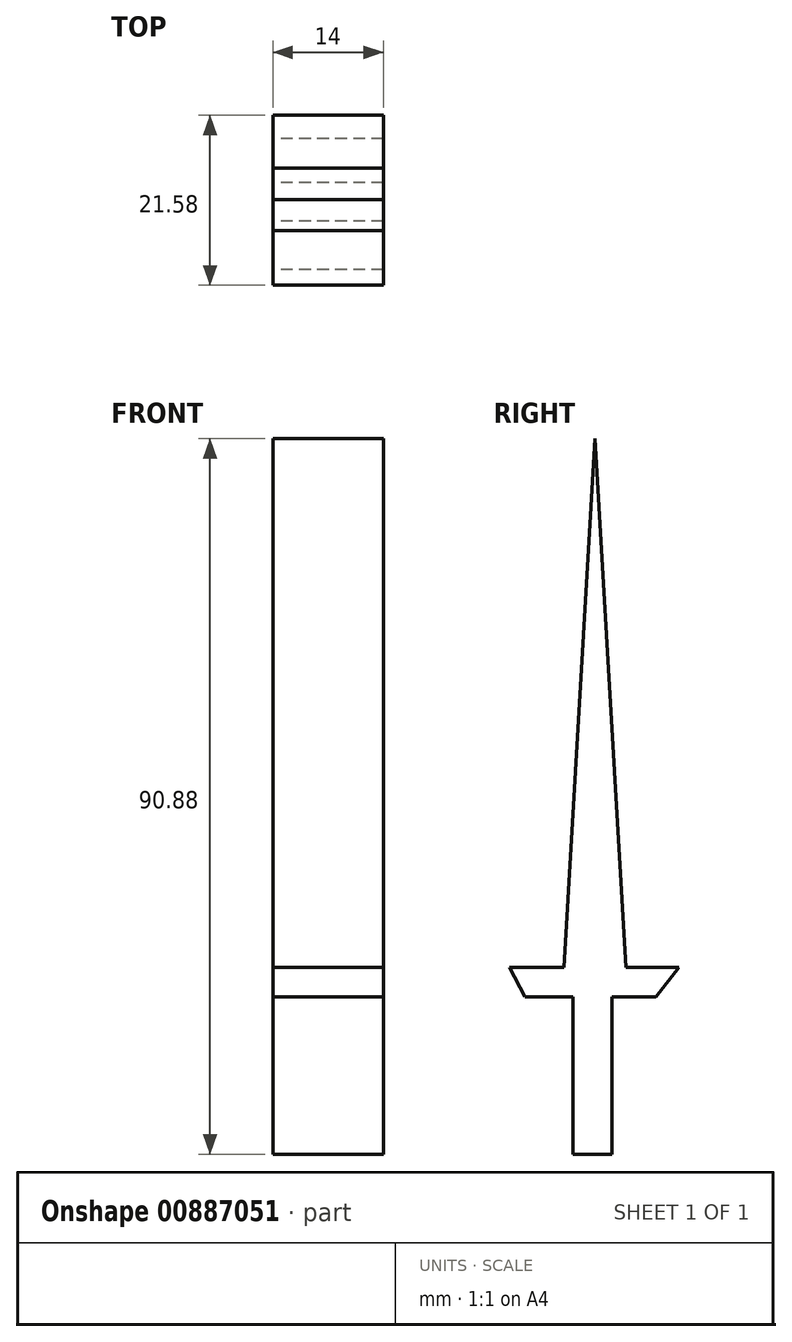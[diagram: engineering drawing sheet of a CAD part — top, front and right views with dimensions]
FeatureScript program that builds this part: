
annotation { "Feature Type Name" : "Feature", "Feature Type Description" : "" }
export const myFeature = defineFeature(function(context is Context, id is Id, definition is map)
    precondition{}
    {
        {
            var Q0;
            Q0=qCreatedBy(makeId("Right.planeOp"),FACE);
            var sketch = newSketch(context, id + "F0", { "sketchPlane" : qUnion([Q0])});
            skLineSegment(sketch, "E0", {"start": v(-10.9, 0) * mm, "end": v(10.7, 0) * mm});
            skLineSegment(sketch, "E1", {"start": v(-10.9, 0) * mm, "end": v(-8.91, -3.71) * mm});
            skLineSegment(sketch, "E2", {"start": v(-8.91, -3.71) * mm, "end": v(7.72, -3.71) * mm});
            skLineSegment(sketch, "E3", {"start": v(7.72, -3.71) * mm, "end": v(10.7, 0) * mm});
            skLineSegment(sketch, "E4", {"start": v(-2.77, -3.71) * mm, "end": v(-2.77, -23.71) * mm});
            skLineSegment(sketch, "E5", {"start": v(2.18, -3.71) * mm, "end": v(2.18, -23.71) * mm});
            skLineSegment(sketch, "E6", {"start": v(-2.77, -23.71) * mm, "end": v(2.18, -23.71) * mm});
            skLineSegment(sketch, "E7", {"start": v(-2.77, -3.71) * mm, "end": v(2.18, -6.49) * mm});
            skLineSegment(sketch, "E8", {"start": v(2.18, -6.49) * mm, "end": v(-2.77, -9.36) * mm});
            skLineSegment(sketch, "E9", {"start": v(-2.77, -9.36) * mm, "end": v(2.18, -11.83) * mm});
            skLineSegment(sketch, "E10", {"start": v(2.18, -11.83) * mm, "end": v(-2.77, -13.71) * mm});
            skLineSegment(sketch, "E11", {"start": v(-2.77, -13.71) * mm, "end": v(2.18, -16.98) * mm});
            skLineSegment(sketch, "E12", {"start": v(2.18, -16.98) * mm, "end": v(-2.77, -19.75) * mm});
            skLineSegment(sketch, "E13", {"start": v(-2.77, -19.75) * mm, "end": v(2.18, -21.34) * mm});
            skLineSegment(sketch, "E14", {"start": v(2.18, -21.34) * mm, "end": v(-2.77, -23.71) * mm});
            skLineSegment(sketch, "E15", {"start": v(2.18, -23.71) * mm, "end": v(-2.77, -21.34) * mm});
            skLineSegment(sketch, "E16", {"start": v(-2.77, -21.34) * mm, "end": v(2.18, -19.75) * mm});
            skLineSegment(sketch, "E17", {"start": v(2.18, -19.75) * mm, "end": v(-2.77, -16.98) * mm});
            skLineSegment(sketch, "E18", {"start": v(-2.77, -16.98) * mm, "end": v(2.18, -13.71) * mm});
            skLineSegment(sketch, "E19", {"start": v(2.18, -13.71) * mm, "end": v(-2.77, -12.03) * mm});
            skLineSegment(sketch, "E20", {"start": v(-2.77, -12.03) * mm, "end": v(2.18, -8.86) * mm});
            skLineSegment(sketch, "E21", {"start": v(2.18, -8.86) * mm, "end": v(-2.77, -6.39) * mm});
            skLineSegment(sketch, "E22", {"start": v(-2.77, -6.39) * mm, "end": v(2.18, -3.71) * mm});
            skLineSegment(sketch, "E23", {"start": v(-3.96, 0) * mm, "end": v(0, 67.17) * mm});
            skLineSegment(sketch, "E24.MirrorCS", {"start": v(3.96, 0) * mm, "end": v(0, 67.17) * mm});
            skSolve(sketch);
        }
        {
            var Q0;
            {var subQ0=sQuery(id+"F0.wireOp",EDGE,"E23");Q0=makeQuery(id+"F0.imprint","IMPRINT",FACE,{"disambiguationData":[TD([[makeQuery(id+"F0.imprint","IMPRINT",EDGE,{"derivedFrom":subQ0}),-1.0]])]});}
            var Q1;
            {var subQ0=sQuery(id+"F0.wireOp",EDGE,"E1");Q1=makeQuery(id+"F0.imprint","IMPRINT",FACE,{"disambiguationData":[TD([[makeQuery(id+"F0.imprint","IMPRINT",EDGE,{"derivedFrom":subQ0}),1.0]])]});}
            var Q2;
            {var subQ0=sQuery(id+"F0.wireOp",EDGE,"E7");var subQ3=sQuery(id+"F0.wireOp",EDGE,"E22");var subQ5=makeQuery(id+"F0.imprint","INTERSECT",VERTEX,{"derivedFrom":[subQ0,subQ3]});Q2=makeQuery(id+"F0.imprint","IMPRINT",FACE,{"disambiguationData":[TD([[makeQuery(id+"F0.imprint","IMPRINT",EDGE,{"disambiguationData":[TD([[subQ5,1.0]])],"derivedFrom":subQ0}),1.0]])]});}
            var Q3;
            {var subQ1=sQuery(id+"F0.wireOp",EDGE,"E7");var subQ3=sQuery(id+"F0.wireOp",EDGE,"E22");var subQ4=makeQuery(id+"F0.imprint","INTERSECT",VERTEX,{"derivedFrom":[subQ1,subQ3]});Q3=makeQuery(id+"F0.imprint","IMPRINT",FACE,{"disambiguationData":[TD([[makeQuery(id+"F0.imprint","IMPRINT",EDGE,{"disambiguationData":[TD([[subQ4,-1.0]])],"derivedFrom":subQ1}),-1.0]])]});}
            var Q4;
            {var subQ0=sQuery(id+"F0.wireOp",EDGE,"E7");var subQ3=sQuery(id+"F0.wireOp",EDGE,"E22");var subQ5=makeQuery(id+"F0.imprint","INTERSECT",VERTEX,{"derivedFrom":[subQ0,subQ3]});Q4=makeQuery(id+"F0.imprint","IMPRINT",FACE,{"disambiguationData":[TD([[makeQuery(id+"F0.imprint","IMPRINT",EDGE,{"disambiguationData":[TD([[subQ5,1.0]])],"derivedFrom":subQ0}),-1.0]])]});}
            var Q5;
            {var subQ0=sQuery(id+"F0.wireOp",EDGE,"E22");var subQ3=sQuery(id+"F0.wireOp",EDGE,"E7");var subQ5=makeQuery(id+"F0.imprint","INTERSECT",VERTEX,{"derivedFrom":[subQ3,subQ0]});Q5=makeQuery(id+"F0.imprint","IMPRINT",FACE,{"disambiguationData":[TD([[makeQuery(id+"F0.imprint","IMPRINT",EDGE,{"disambiguationData":[TD([[subQ5,-1.0]])],"derivedFrom":subQ3}),1.0]])]});}
            var Q6;
            {var subQ0=sQuery(id+"F0.wireOp",EDGE,"E8");var subQ3=sQuery(id+"F0.wireOp",EDGE,"E21");var subQ5=makeQuery(id+"F0.imprint","INTERSECT",VERTEX,{"derivedFrom":[subQ0,subQ3]});Q6=makeQuery(id+"F0.imprint","IMPRINT",FACE,{"disambiguationData":[TD([[makeQuery(id+"F0.imprint","IMPRINT",EDGE,{"disambiguationData":[TD([[subQ5,-1.0]])],"derivedFrom":subQ0}),-1.0]])]});}
            var Q7;
            {var subQ0=sQuery(id+"F0.wireOp",EDGE,"E8");var subQ3=sQuery(id+"F0.wireOp",EDGE,"E21");var subQ5=makeQuery(id+"F0.imprint","INTERSECT",VERTEX,{"derivedFrom":[subQ0,subQ3]});Q7=makeQuery(id+"F0.imprint","IMPRINT",FACE,{"disambiguationData":[TD([[makeQuery(id+"F0.imprint","IMPRINT",EDGE,{"disambiguationData":[TD([[subQ5,1.0]])],"derivedFrom":subQ0}),1.0]])]});}
            var Q8;
            {var subQ1=sQuery(id+"F0.wireOp",EDGE,"E8");var subQ3=sQuery(id+"F0.wireOp",EDGE,"E21");var subQ4=makeQuery(id+"F0.imprint","INTERSECT",VERTEX,{"derivedFrom":[subQ1,subQ3]});Q8=makeQuery(id+"F0.imprint","IMPRINT",FACE,{"disambiguationData":[TD([[makeQuery(id+"F0.imprint","IMPRINT",EDGE,{"disambiguationData":[TD([[subQ4,-1.0]])],"derivedFrom":subQ1}),1.0]])]});}
            var Q9;
            {var subQ0=sQuery(id+"F0.wireOp",EDGE,"E9");var subQ3=sQuery(id+"F0.wireOp",EDGE,"E20");var subQ5=makeQuery(id+"F0.imprint","INTERSECT",VERTEX,{"derivedFrom":[subQ0,subQ3]});Q9=makeQuery(id+"F0.imprint","IMPRINT",FACE,{"disambiguationData":[TD([[makeQuery(id+"F0.imprint","IMPRINT",EDGE,{"disambiguationData":[TD([[subQ5,1.0]])],"derivedFrom":subQ0}),-1.0]])]});}
            var Q10;
            {var subQ0=sQuery(id+"F0.wireOp",EDGE,"E9");var subQ3=sQuery(id+"F0.wireOp",EDGE,"E20");var subQ5=makeQuery(id+"F0.imprint","INTERSECT",VERTEX,{"derivedFrom":[subQ0,subQ3]});Q10=makeQuery(id+"F0.imprint","IMPRINT",FACE,{"disambiguationData":[TD([[makeQuery(id+"F0.imprint","IMPRINT",EDGE,{"disambiguationData":[TD([[subQ5,-1.0]])],"derivedFrom":subQ0}),1.0]])]});}
            var Q11;
            {var subQ1=sQuery(id+"F0.wireOp",EDGE,"E9");var subQ3=sQuery(id+"F0.wireOp",EDGE,"E20");var subQ4=makeQuery(id+"F0.imprint","INTERSECT",VERTEX,{"derivedFrom":[subQ1,subQ3]});Q11=makeQuery(id+"F0.imprint","IMPRINT",FACE,{"disambiguationData":[TD([[makeQuery(id+"F0.imprint","IMPRINT",EDGE,{"disambiguationData":[TD([[subQ4,-1.0]])],"derivedFrom":subQ1}),-1.0]])]});}
            var Q12;
            {var subQ0=sQuery(id+"F0.wireOp",EDGE,"E10");var subQ3=sQuery(id+"F0.wireOp",EDGE,"E19");var subQ5=makeQuery(id+"F0.imprint","INTERSECT",VERTEX,{"derivedFrom":[subQ0,subQ3]});Q12=makeQuery(id+"F0.imprint","IMPRINT",FACE,{"disambiguationData":[TD([[makeQuery(id+"F0.imprint","IMPRINT",EDGE,{"disambiguationData":[TD([[subQ5,1.0]])],"derivedFrom":subQ0}),1.0]])]});}
            var Q13;
            {var subQ0=sQuery(id+"F0.wireOp",EDGE,"E10");var subQ3=sQuery(id+"F0.wireOp",EDGE,"E19");var subQ5=makeQuery(id+"F0.imprint","INTERSECT",VERTEX,{"derivedFrom":[subQ0,subQ3]});Q13=makeQuery(id+"F0.imprint","IMPRINT",FACE,{"disambiguationData":[TD([[makeQuery(id+"F0.imprint","IMPRINT",EDGE,{"disambiguationData":[TD([[subQ5,-1.0]])],"derivedFrom":subQ0}),-1.0]])]});}
            var Q14;
            {var subQ0=sQuery(id+"F0.wireOp",EDGE,"E11");var subQ3=sQuery(id+"F0.wireOp",EDGE,"E18");var subQ5=makeQuery(id+"F0.imprint","INTERSECT",VERTEX,{"derivedFrom":[subQ0,subQ3]});Q14=makeQuery(id+"F0.imprint","IMPRINT",FACE,{"disambiguationData":[TD([[makeQuery(id+"F0.imprint","IMPRINT",EDGE,{"disambiguationData":[TD([[subQ5,1.0]])],"derivedFrom":subQ0}),-1.0]])]});}
            var Q15;
            {var subQ0=sQuery(id+"F0.wireOp",EDGE,"E11");var subQ3=sQuery(id+"F0.wireOp",EDGE,"E18");var subQ5=makeQuery(id+"F0.imprint","INTERSECT",VERTEX,{"derivedFrom":[subQ0,subQ3]});Q15=makeQuery(id+"F0.imprint","IMPRINT",FACE,{"disambiguationData":[TD([[makeQuery(id+"F0.imprint","IMPRINT",EDGE,{"disambiguationData":[TD([[subQ5,-1.0]])],"derivedFrom":subQ0}),1.0]])]});}
            var Q16;
            {var subQ1=sQuery(id+"F0.wireOp",EDGE,"E11");var subQ3=sQuery(id+"F0.wireOp",EDGE,"E18");var subQ4=makeQuery(id+"F0.imprint","INTERSECT",VERTEX,{"derivedFrom":[subQ1,subQ3]});Q16=makeQuery(id+"F0.imprint","IMPRINT",FACE,{"disambiguationData":[TD([[makeQuery(id+"F0.imprint","IMPRINT",EDGE,{"disambiguationData":[TD([[subQ4,-1.0]])],"derivedFrom":subQ1}),-1.0]])]});}
            var Q17;
            {var subQ0=sQuery(id+"F0.wireOp",EDGE,"E12");var subQ3=sQuery(id+"F0.wireOp",EDGE,"E17");var subQ5=makeQuery(id+"F0.imprint","INTERSECT",VERTEX,{"derivedFrom":[subQ0,subQ3]});Q17=makeQuery(id+"F0.imprint","IMPRINT",FACE,{"disambiguationData":[TD([[makeQuery(id+"F0.imprint","IMPRINT",EDGE,{"disambiguationData":[TD([[subQ5,-1.0]])],"derivedFrom":subQ0}),-1.0]])]});}
            var Q18;
            {var subQ0=sQuery(id+"F0.wireOp",EDGE,"E12");var subQ3=sQuery(id+"F0.wireOp",EDGE,"E17");var subQ5=makeQuery(id+"F0.imprint","INTERSECT",VERTEX,{"derivedFrom":[subQ0,subQ3]});Q18=makeQuery(id+"F0.imprint","IMPRINT",FACE,{"disambiguationData":[TD([[makeQuery(id+"F0.imprint","IMPRINT",EDGE,{"disambiguationData":[TD([[subQ5,1.0]])],"derivedFrom":subQ0}),1.0]])]});}
            var Q19;
            {var subQ0=sQuery(id+"F0.wireOp",EDGE,"E13");var subQ3=sQuery(id+"F0.wireOp",EDGE,"E16");var subQ5=makeQuery(id+"F0.imprint","INTERSECT",VERTEX,{"derivedFrom":[subQ0,subQ3]});Q19=makeQuery(id+"F0.imprint","IMPRINT",FACE,{"disambiguationData":[TD([[makeQuery(id+"F0.imprint","IMPRINT",EDGE,{"disambiguationData":[TD([[subQ5,1.0]])],"derivedFrom":subQ0}),-1.0]])]});}
            var Q20;
            {var subQ1=sQuery(id+"F0.wireOp",EDGE,"E12");var subQ3=sQuery(id+"F0.wireOp",EDGE,"E17");var subQ4=makeQuery(id+"F0.imprint","INTERSECT",VERTEX,{"derivedFrom":[subQ1,subQ3]});Q20=makeQuery(id+"F0.imprint","IMPRINT",FACE,{"disambiguationData":[TD([[makeQuery(id+"F0.imprint","IMPRINT",EDGE,{"disambiguationData":[TD([[subQ4,-1.0]])],"derivedFrom":subQ1}),1.0]])]});}
            var Q21;
            {var subQ0=sQuery(id+"F0.wireOp",EDGE,"E13");var subQ3=sQuery(id+"F0.wireOp",EDGE,"E16");var subQ5=makeQuery(id+"F0.imprint","INTERSECT",VERTEX,{"derivedFrom":[subQ0,subQ3]});Q21=makeQuery(id+"F0.imprint","IMPRINT",FACE,{"disambiguationData":[TD([[makeQuery(id+"F0.imprint","IMPRINT",EDGE,{"disambiguationData":[TD([[subQ5,-1.0]])],"derivedFrom":subQ0}),1.0]])]});}
            var Q22;
            {var subQ1=sQuery(id+"F0.wireOp",EDGE,"E13");var subQ3=sQuery(id+"F0.wireOp",EDGE,"E16");var subQ4=makeQuery(id+"F0.imprint","INTERSECT",VERTEX,{"derivedFrom":[subQ1,subQ3]});Q22=makeQuery(id+"F0.imprint","IMPRINT",FACE,{"disambiguationData":[TD([[makeQuery(id+"F0.imprint","IMPRINT",EDGE,{"disambiguationData":[TD([[subQ4,-1.0]])],"derivedFrom":subQ1}),-1.0]])]});}
            var Q23;
            {var subQ0=sQuery(id+"F0.wireOp",EDGE,"E14");var subQ3=sQuery(id+"F0.wireOp",EDGE,"E15");var subQ5=makeQuery(id+"F0.imprint","INTERSECT",VERTEX,{"derivedFrom":[subQ0,subQ3]});Q23=makeQuery(id+"F0.imprint","IMPRINT",FACE,{"disambiguationData":[TD([[makeQuery(id+"F0.imprint","IMPRINT",EDGE,{"disambiguationData":[TD([[subQ5,-1.0]])],"derivedFrom":subQ0}),-1.0]])]});}
            var Q24;
            {var subQ0=sQuery(id+"F0.wireOp",EDGE,"E6");Q24=makeQuery(id+"F0.imprint","IMPRINT",FACE,{"disambiguationData":[TD([[makeQuery(id+"F0.imprint","IMPRINT",EDGE,{"derivedFrom":subQ0}),1.0]])]});}
            var Q25;
            {var subQ0=sQuery(id+"F0.wireOp",EDGE,"E15");var subQ3=sQuery(id+"F0.wireOp",EDGE,"E14");var subQ5=makeQuery(id+"F0.imprint","INTERSECT",VERTEX,{"derivedFrom":[subQ3,subQ0]});Q25=makeQuery(id+"F0.imprint","IMPRINT",FACE,{"disambiguationData":[TD([[makeQuery(id+"F0.imprint","IMPRINT",EDGE,{"disambiguationData":[TD([[subQ5,1.0]])],"derivedFrom":subQ3}),1.0]])]});}
            var Q26;
            {var subQ1=sQuery(id+"F0.wireOp",EDGE,"E10");var subQ3=sQuery(id+"F0.wireOp",EDGE,"E19");var subQ4=makeQuery(id+"F0.imprint","INTERSECT",VERTEX,{"derivedFrom":[subQ1,subQ3]});Q26=makeQuery(id+"F0.imprint","IMPRINT",FACE,{"disambiguationData":[TD([[makeQuery(id+"F0.imprint","IMPRINT",EDGE,{"disambiguationData":[TD([[subQ4,-1.0]])],"derivedFrom":subQ1}),1.0]])]});}
            extrude(context, id + "F1", {"entities" : qUnion([Q0, Q1, Q2, Q3, Q4, Q5, Q6, Q7, Q8, Q9, Q10, Q11, Q12, Q13, Q14, Q15, Q16, Q17, Q18, Q19, Q20, Q21, Q22, Q23, Q24, Q25, Q26]), "depth" : 14 * mm, "offsetDistance" : 25.4 * mm});
        }
    });
